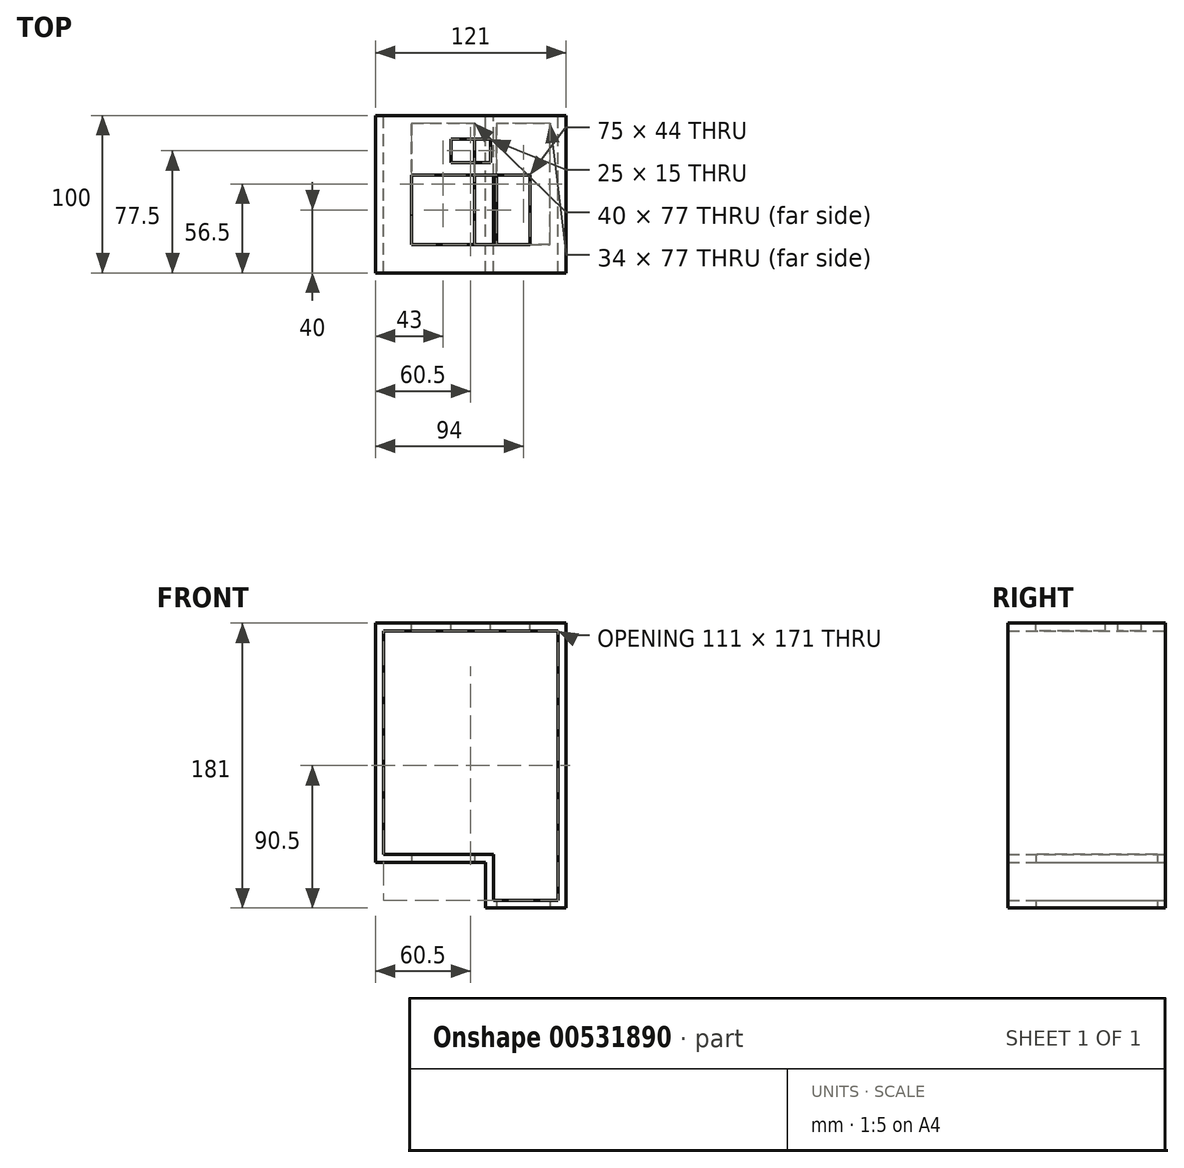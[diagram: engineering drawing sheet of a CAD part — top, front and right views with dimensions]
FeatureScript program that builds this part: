
annotation { "Feature Type Name" : "Feature", "Feature Type Description" : "" }
export const myFeature = defineFeature(function(context is Context, id is Id, definition is map)
    precondition{}
    {
        {
            var Q0;
            Q0=qCreatedBy(makeId("Front.planeOp"),FACE);
            var sketch = newSketch(context, id + "F0", { "sketchPlane" : qUnion([Q0])});
            skLineSegment(sketch, "E0.bottom", {"start": v(55.5, 71) * mm, "end": v(-55.5, 71) * mm, "construction": true});
            skLineSegment(sketch, "E0.top", {"start": v(55.5, -71) * mm, "end": v(-55.5, -71) * mm, "construction": true});
            skLineSegment(sketch, "E0.left", {"start": v(55.5, 71) * mm, "end": v(55.5, -71) * mm, "construction": true});
            skLineSegment(sketch, "E0.right", {"start": v(-55.5, 71) * mm, "end": v(-55.5, -71) * mm, "construction": true});
            skPoint(sketch, "E0.middle", {"position": v(0, 0) * mm});
            skLineSegment(sketch, "E1.bottom", {"start": v(55.5, -71) * mm, "end": v(14.5, -71) * mm, "construction": true});
            skLineSegment(sketch, "E1.top", {"start": v(55.5, -100) * mm, "end": v(14.5, -100) * mm, "construction": true});
            skLineSegment(sketch, "E1.left", {"start": v(55.5, -71) * mm, "end": v(55.5, -100) * mm, "construction": true});
            skLineSegment(sketch, "E1.right", {"start": v(14.5, -71) * mm, "end": v(14.5, -100) * mm, "construction": true});
            skLineSegment(sketch, "E2.bottom", {"start": v(-55.5, 71) * mm, "end": v(-60.5, 71) * mm});
            skLineSegment(sketch, "E2.top", {"start": v(-55.5, -71) * mm, "end": v(-60.5, -71) * mm});
            skLineSegment(sketch, "E2.left", {"start": v(-55.5, 71) * mm, "end": v(-55.5, -71) * mm});
            skLineSegment(sketch, "E2.right", {"start": v(-60.5, 71) * mm, "end": v(-60.5, -71) * mm});
            skLineSegment(sketch, "E3.bottom", {"start": v(-60.5, -71) * mm, "end": v(14.5, -71) * mm});
            skLineSegment(sketch, "E3.top", {"start": v(-60.5, -76) * mm, "end": v(14.5, -76) * mm});
            skLineSegment(sketch, "E3.left", {"start": v(-60.5, -71) * mm, "end": v(-60.5, -76) * mm});
            skLineSegment(sketch, "E3.right", {"start": v(14.5, -71) * mm, "end": v(14.5, -76) * mm});
            skLineSegment(sketch, "E4.bottom", {"start": v(14.5, -76) * mm, "end": v(9.5, -76) * mm});
            skLineSegment(sketch, "E4.top", {"start": v(14.5, -100) * mm, "end": v(9.5, -100) * mm});
            skLineSegment(sketch, "E4.left", {"start": v(14.5, -76) * mm, "end": v(14.5, -100) * mm});
            skLineSegment(sketch, "E4.right", {"start": v(9.5, -76) * mm, "end": v(9.5, -100) * mm});
            skLineSegment(sketch, "E5.bottom", {"start": v(9.5, -100) * mm, "end": v(55.5, -100) * mm});
            skLineSegment(sketch, "E5.top", {"start": v(9.5, -105) * mm, "end": v(55.5, -105) * mm});
            skLineSegment(sketch, "E5.left", {"start": v(9.5, -100) * mm, "end": v(9.5, -105) * mm});
            skLineSegment(sketch, "E5.right", {"start": v(55.5, -100) * mm, "end": v(55.5, -105) * mm});
            skLineSegment(sketch, "E6.bottom", {"start": v(55.5, -105) * mm, "end": v(60.5, -105) * mm});
            skLineSegment(sketch, "E6.top", {"start": v(55.5, 71) * mm, "end": v(60.5, 71) * mm});
            skLineSegment(sketch, "E6.left", {"start": v(55.5, -105) * mm, "end": v(55.5, 71) * mm});
            skLineSegment(sketch, "E6.right", {"start": v(60.5, -105) * mm, "end": v(60.5, 71) * mm});
            skLineSegment(sketch, "E7.bottom", {"start": v(60.5, 71) * mm, "end": v(-60.5, 71) * mm});
            skLineSegment(sketch, "E7.top", {"start": v(60.5, 76) * mm, "end": v(-60.5, 76) * mm});
            skLineSegment(sketch, "E7.left", {"start": v(60.5, 71) * mm, "end": v(60.5, 76) * mm});
            skLineSegment(sketch, "E7.right", {"start": v(-60.5, 71) * mm, "end": v(-60.5, 76) * mm});
            skSolve(sketch);
        }
        {
            var Q0;
            Q0 = qSketchRegion(id + "F0", true);
            extrude(context, id + "F1", {"entities" : qUnion([Q0]), "depth" : 100 * mm, "offsetDistance" : 25 * mm});
        }
        {
            var Q0;
            Q0=makeQuery(id+"F1.opExtrude","SWEPT_FACE",FACE,{"disambiguationData":[OSD([sQuery(id+"F0.wireOp",EDGE,"E7.top")])]});
            var sketch = newSketch(context, id + "F2", { "sketchPlane" : qUnion([Q0])});
            skLineSegment(sketch, "E8.bottom", {"start": v(37.5, -82) * mm, "end": v(-37.5, -82) * mm});
            skLineSegment(sketch, "E8.top", {"start": v(37.5, -38) * mm, "end": v(-37.5, -38) * mm});
            skLineSegment(sketch, "E8.left", {"start": v(37.5, -82) * mm, "end": v(37.5, -38) * mm});
            skLineSegment(sketch, "E8.right", {"start": v(-37.5, -82) * mm, "end": v(-37.5, -38) * mm});
            skSolve(sketch);
        }
        {
            var Q0;
            Q0 = qSketchRegion(id + "F2", true);
            extrude(context, id + "F3", {"entities" : qUnion([Q0]), "operationType" : NewBodyOperationType.REMOVE, "oppositeDirection" : true, "depth" : 25 * mm, "offsetDistance" : 25 * mm});
        }
        {
            var Q0;
            Q0=makeQuery(id+"F1.opExtrude","SWEPT_FACE",FACE,{"disambiguationData":[OSD([sQuery(id+"F0.wireOp",EDGE,"E5.top"),sQuery(id+"F0.wireOp",EDGE,"E6.bottom")])]});
            var sketch = newSketch(context, id + "F4", { "sketchPlane" : qUnion([Q0])});
            skLineSegment(sketch, "E9.bottom", {"start": v(50.5, 5) * mm, "end": v(16.5, 5) * mm});
            skLineSegment(sketch, "E9.top", {"start": v(50.5, 82) * mm, "end": v(16.5, 82) * mm});
            skLineSegment(sketch, "E9.left", {"start": v(50.5, 5) * mm, "end": v(50.5, 82) * mm});
            skLineSegment(sketch, "E9.right", {"start": v(16.5, 5) * mm, "end": v(16.5, 82) * mm});
            skSolve(sketch);
        }
        {
            var Q0;
            Q0 = qSketchRegion(id + "F4", true);
            extrude(context, id + "F5", {"entities" : qUnion([Q0]), "operationType" : NewBodyOperationType.REMOVE, "oppositeDirection" : true, "depth" : 25 * mm, "offsetDistance" : 25 * mm});
        }
        {
            var Q0;
            Q0=makeQuery(id+"F1.opExtrude","SWEPT_FACE",FACE,{"disambiguationData":[OSD([sQuery(id+"F0.wireOp",EDGE,"E3.top")])]});
            var sketch = newSketch(context, id + "F6", { "sketchPlane" : qUnion([Q0])});
            skSolve(sketch);
        }
        {
            var Q0;
            {var subQ0=sQuery(id+"F0.wireOp",EDGE,"E3.top");Q0=makeQuery(id+"F6.imprint","IMPRINT",FACE,{"disambiguationData":[TD([[makeQuery(id+"F6.imprint","IMPRINT",EDGE,{"derivedFrom":makeQuery(id+"F1.opExtrude","CAP_EDGE",EDGE,{"disambiguationData":[OSD([subQ0])],"isStart":true})}),1.0]])]});}
            var sketch = newSketch(context, id + "F7", { "sketchPlane" : qUnion([Q0])});
            skLineSegment(sketch, "E10.bottom", {"start": v(-37.5, 82) * mm, "end": v(2.5, 82) * mm});
            skLineSegment(sketch, "E10.top", {"start": v(-37.5, 5) * mm, "end": v(2.5, 5) * mm});
            skLineSegment(sketch, "E10.left", {"start": v(-37.5, 82) * mm, "end": v(-37.5, 5) * mm});
            skLineSegment(sketch, "E10.right", {"start": v(2.5, 82) * mm, "end": v(2.5, 5) * mm});
            skSolve(sketch);
        }
        {
            var Q0;
            Q0 = qSketchRegion(id + "F7", true);
            extrude(context, id + "F8", {"entities" : qUnion([Q0]), "operationType" : NewBodyOperationType.REMOVE, "oppositeDirection" : true, "depth" : 25 * mm, "offsetDistance" : 25 * mm});
        }
        {
            var Q0;
            Q0=makeQuery(id+"F1.opExtrude","SWEPT_FACE",FACE,{"disambiguationData":[OSD([sQuery(id+"F0.wireOp",EDGE,"E7.top")])]});
            var sketch = newSketch(context, id + "F9", { "sketchPlane" : qUnion([Q0])});
            skLineSegment(sketch, "E11.bottom", {"start": v(12.5, -30) * mm, "end": v(-12.5, -30) * mm});
            skLineSegment(sketch, "E11.top", {"start": v(12.5, -15) * mm, "end": v(-12.5, -15) * mm});
            skLineSegment(sketch, "E11.left", {"start": v(12.5, -30) * mm, "end": v(12.5, -15) * mm});
            skLineSegment(sketch, "E11.right", {"start": v(-12.5, -30) * mm, "end": v(-12.5, -15) * mm});
            skPoint(sketch, "E11.middle", {"position": v(0, -22.5) * mm});
            skSolve(sketch);
        }
        {
            var Q0;
            Q0 = qSketchRegion(id + "F9", true);
            extrude(context, id + "F10", {"entities" : qUnion([Q0]), "operationType" : NewBodyOperationType.REMOVE, "oppositeDirection" : true, "depth" : 25 * mm, "offsetDistance" : 25 * mm});
        }
    });
